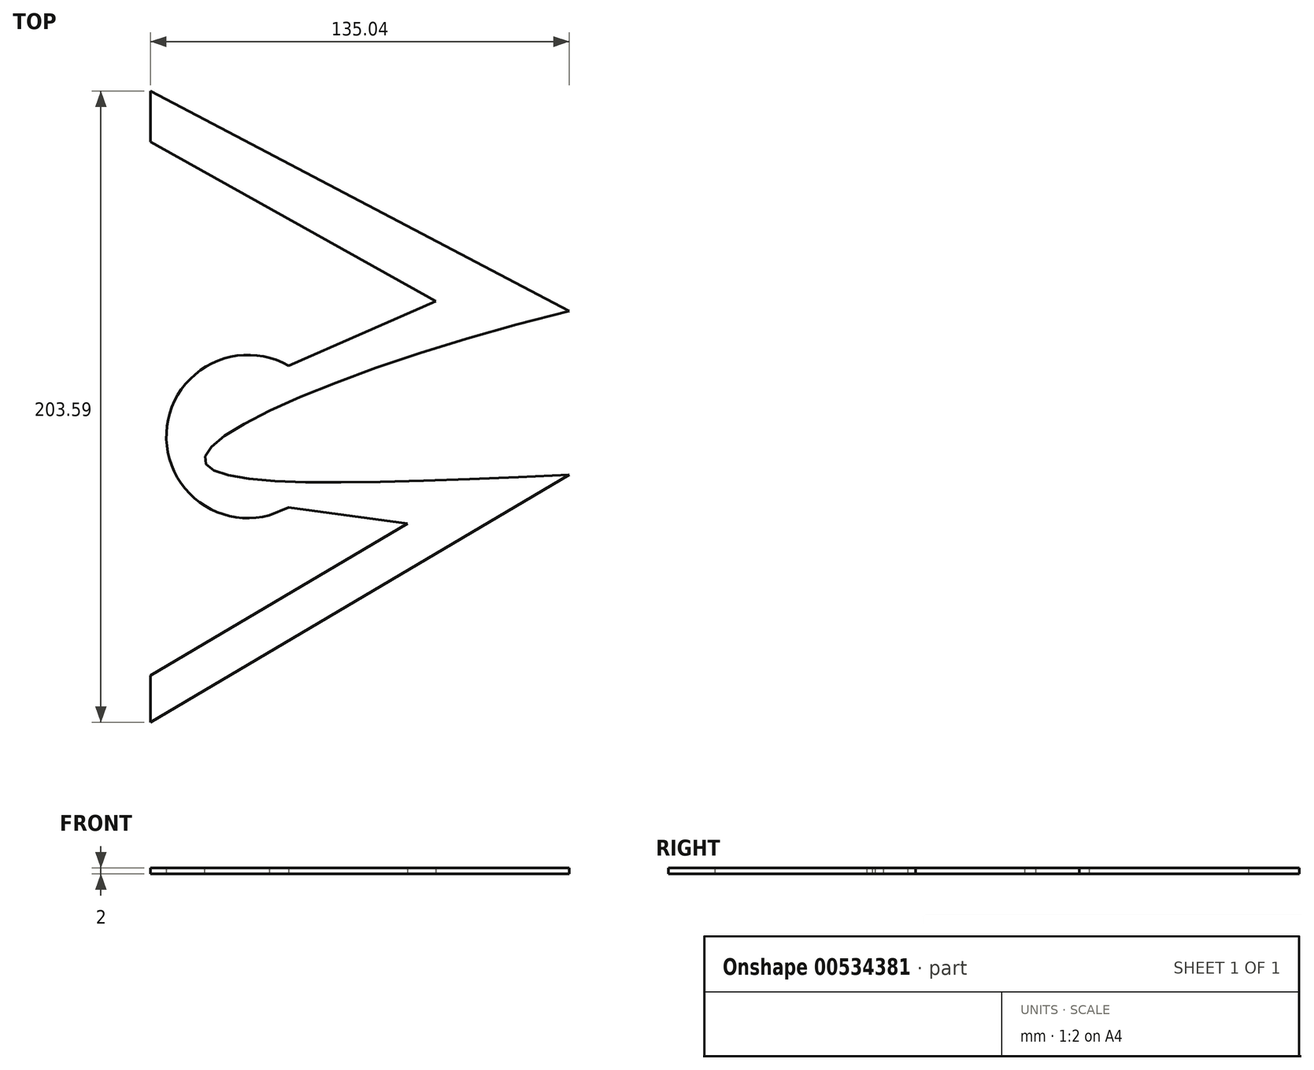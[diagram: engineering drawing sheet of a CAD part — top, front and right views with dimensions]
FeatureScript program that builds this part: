
annotation { "Feature Type Name" : "Feature", "Feature Type Description" : "" }
export const myFeature = defineFeature(function(context is Context, id is Id, definition is map)
    precondition{}
    {
        {
            var Q0;
            Q0=qCreatedBy(makeId("Top.planeOp"),FACE);
            var sketch = newSketch(context, id + "F0", { "sketchPlane" : qUnion([Q0])});
            skFitSpline(sketch, "E0", {"points": [v(170.92, -25.91) * mm, v(60.86, 23.87) * mm, v(-209.08, -41.36) * mm, v(-7.42, -43.48) * mm, v(170.92, -25.91) * mm]});
            skLineSegment(sketch, "E1", {"start": v(-209.08, -41.36) * mm, "end": v(170.92, -25.91) * mm, "construction": true});
            skLineSegment(sketch, "E2", {"start": v(-91.6, 5.72) * mm, "end": v(-226.64, 76.62) * mm});
            skLineSegment(sketch, "E3", {"start": v(-226.64, 76.62) * mm, "end": v(-226.64, 25.7) * mm});
            skLineSegment(sketch, "E4", {"start": v(-226.64, 25.7) * mm, "end": v(-182.1, -11.97) * mm});
            skLineSegment(sketch, "E5", {"start": v(-91.6, -47.1) * mm, "end": v(-226.64, -126.97) * mm});
            skLineSegment(sketch, "E6", {"start": v(-226.64, -126.97) * mm, "end": v(-226.64, -76.1) * mm});
            skLineSegment(sketch, "E7", {"start": v(-226.64, -76.1) * mm, "end": v(-182.1, -57.63) * mm});
            skArc(sketch, "E8", {"start": v(-182.1, -11.97) * mm, "mid": v(-221.55, -34.8) * mm, "end": v(-182.1, -57.63) * mm});
            skLineSegment(sketch, "E9", {"start": v(-226.64, 60.31) * mm, "end": v(-134.55, 8.89) * mm});
            skLineSegment(sketch, "E10", {"start": v(-134.55, 8.89) * mm, "end": v(-182.1, -11.97) * mm});
            skLineSegment(sketch, "E11", {"start": v(-226.64, -111.97) * mm, "end": v(-143.68, -62.9) * mm});
            skLineSegment(sketch, "E12", {"start": v(-143.68, -62.9) * mm, "end": v(-182.1, -57.63) * mm});
            skSolve(sketch);
        }
        {
            var Q0;
            {var subQ1=sQuery(id+"F0.wireOp",EDGE,"E2");Q0=makeQuery(id+"F0.imprint","IMPRINT",FACE,{"disambiguationData":[TD([[makeQuery(id+"F0.imprint","IMPRINT",EDGE,{"derivedFrom":subQ1}),1.0]])]});}
            extrude(context, id + "F1", {"entities" : qUnion([Q0]), "depth" : 2 * mm, "offsetDistance" : 25 * mm});
        }
    });
